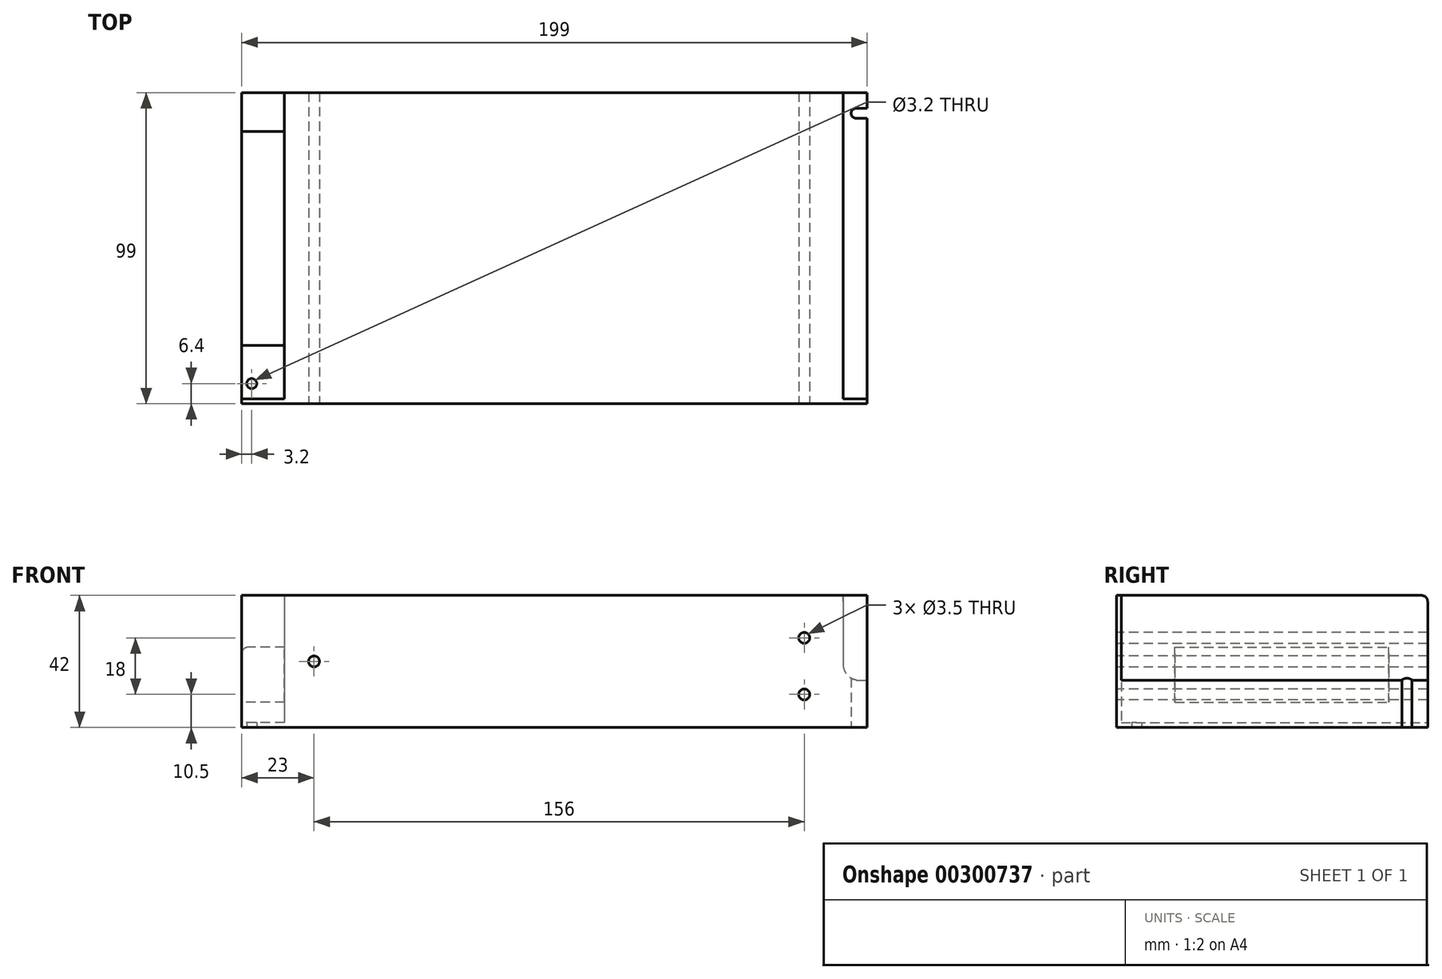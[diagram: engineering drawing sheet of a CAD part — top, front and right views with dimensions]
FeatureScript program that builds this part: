
annotation { "Feature Type Name" : "Feature", "Feature Type Description" : "" }
export const myFeature = defineFeature(function(context is Context, id is Id, definition is map)
    precondition{}
    {
        {
            var Q0;
            Q0=qCreatedBy(makeId("Top.planeOp"),FACE);
            var sketch = newSketch(context, id + "F0", { "sketchPlane" : qUnion([Q0])});
            skLineSegment(sketch, "E0.bottom", {"start": v(-99.5, 49) * mm, "end": v(99.5, 49) * mm});
            skLineSegment(sketch, "E0.top", {"start": v(-99.5, -49) * mm, "end": v(99.5, -49) * mm});
            skLineSegment(sketch, "E0.left", {"start": v(-99.5, 49) * mm, "end": v(-99.5, -49) * mm});
            skLineSegment(sketch, "E0.right", {"start": v(99.5, 49) * mm, "end": v(99.5, -49) * mm});
            skPoint(sketch, "E0.middle", {"position": v(0, 0) * mm});
            skSolve(sketch);
        }
        {
            var Q0;
            Q0=qCreatedBy(makeId("Front.planeOp"),FACE);
            var sketch = newSketch(context, id + "F1", { "sketchPlane" : qUnion([Q0])});
            skLineSegment(sketch, "E1.bottom", {"start": v(-99.5, 21) * mm, "end": v(99.5, 21) * mm});
            skLineSegment(sketch, "E1.top", {"start": v(-99.5, -21) * mm, "end": v(99.5, -21) * mm});
            skLineSegment(sketch, "E1.left", {"start": v(-99.5, 21) * mm, "end": v(-99.5, -21) * mm});
            skLineSegment(sketch, "E1.right", {"start": v(99.5, 21) * mm, "end": v(99.5, -21) * mm});
            skPoint(sketch, "E1.middle", {"position": v(0, 0) * mm});
            skCircle(sketch, "E2", {"center": v(-76.5, 0) * mm, "radius": 1.75 * mm});
            skCircle(sketch, "E3", {"center": v(79.5, 7.5) * mm, "radius": 1.75 * mm});
            skCircle(sketch, "E4.MirrorC", {"center": v(79.5, -10.5) * mm, "radius": 1.75 * mm});
            skSolve(sketch);
        }
        {
            var Q0;
            Q0=makeQuery(id+"F1.imprint","IMPRINT",FACE,{"disambiguationData":[TD([[makeQuery(id+"F1.imprint","IMPRINT",EDGE,{"derivedFrom":sQuery(id+"F1.wireOp",EDGE,"E1.bottom")}),-1.0]])]});
            extrude(context, id + "F2", {"entities" : qUnion([Q0]), "oppositeDirection" : true, "depth" : 99 * mm});
        }
        {
            var Q0;
            Q0=makeQuery(id+"F2.opExtrude","SWEPT_FACE",FACE,{"disambiguationData":[OSD([sQuery(id+"F1.wireOp",EDGE,"E1.right")])]});
            cPlane(context, id + "F3", {"entities" : qUnion([Q0]), "cplaneType" : CPlaneType.OFFSET, "offset" : 0 * mm, "width" : 150 * mm, "height" : 150 * mm});
        }
        {
            var Q0;
            Q0=qCreatedBy(id+"F3.planeOp",FACE);
            var sketch = newSketch(context, id + "F4", { "sketchPlane" : qUnion([Q0])});
            skLineSegment(sketch, "E5.bottom", {"start": v(99, 21) * mm, "end": v(1.5, 21) * mm});
            skLineSegment(sketch, "E5.top", {"start": v(99, -6) * mm, "end": v(1.5, -6) * mm});
            skLineSegment(sketch, "E5.left", {"start": v(99, 21) * mm, "end": v(99, -6) * mm});
            skLineSegment(sketch, "E5.right", {"start": v(1.5, 21) * mm, "end": v(1.5, -6) * mm});
            skSolve(sketch);
        }
        {
            var Q0;
            Q0 = qSketchRegion(id + "F4", true);
            extrude(context, id + "F5", {"entities" : qUnion([Q0]), "operationType" : NewBodyOperationType.REMOVE, "oppositeDirection" : true, "depth" : 7.6 * mm});
        }
        {
            var Q0;
            Q0=makeQuery(id+"F5.boolean.opBoolean","COPY",EDGE,{"derivedFrom":makeQuery(id+"F5.opExtrude","CAP_EDGE",EDGE,{"disambiguationData":[OSD([sQuery(id+"F4.wireOp",EDGE,"E5.top")])],"isStart":false})});
            fillet(context, id + "F6", {"entities" : qUnion([Q0]), "radius" : 5 * mm, "tangentPropagation" : true, "allowEdgeOverflow" : false});
        }
        {
            var Q0;
            Q0=makeQuery(id+"F2.opExtrude","SWEPT_FACE",FACE,{"disambiguationData":[OSD([sQuery(id+"F1.wireOp",EDGE,"E1.left")])]});
            cPlane(context, id + "F7", {"entities" : qUnion([Q0]), "cplaneType" : CPlaneType.OFFSET, "offset" : 0 * mm, "width" : 150 * mm, "height" : 150 * mm});
        }
        {
            var Q0;
            Q0=qCreatedBy(id+"F7.planeOp",FACE);
            var sketch = newSketch(context, id + "F8", { "sketchPlane" : qUnion([Q0])});
            skLineSegment(sketch, "E6.bottom", {"start": v(-1.5, 21) * mm, "end": v(-99, 21) * mm});
            skLineSegment(sketch, "E6.top", {"start": v(-1.5, -19.5) * mm, "end": v(-99, -19.5) * mm});
            skLineSegment(sketch, "E6.left", {"start": v(-1.5, 21) * mm, "end": v(-1.5, -19.5) * mm});
            skLineSegment(sketch, "E6.right", {"start": v(-99, 21) * mm, "end": v(-99, -19.5) * mm});
            skSolve(sketch);
        }
        {
            var Q0;
            Q0 = qSketchRegion(id + "F8", true);
            extrude(context, id + "F9", {"entities" : qUnion([Q0]), "operationType" : NewBodyOperationType.REMOVE, "oppositeDirection" : true, "depth" : 13.6 * mm});
        }
        {
            var Q0;
            Q0=qCreatedBy(id+"F7.planeOp",FACE);
            var sketch = newSketch(context, id + "F10", { "sketchPlane" : qUnion([Q0])});
            skLineSegment(sketch, "E7.bottom", {"start": v(-86.6, 4.5) * mm, "end": v(-18.6, 4.5) * mm});
            skLineSegment(sketch, "E7.top", {"start": v(-86.6, -13) * mm, "end": v(-18.6, -13) * mm});
            skLineSegment(sketch, "E7.left", {"start": v(-86.6, 4.5) * mm, "end": v(-86.6, -13) * mm});
            skLineSegment(sketch, "E7.right", {"start": v(-18.6, 4.5) * mm, "end": v(-18.6, -13) * mm});
            skSolve(sketch);
        }
        {
            var Q0;
            Q0 = qSketchRegion(id + "F10", true);
            extrude(context, id + "F11", {"entities" : qUnion([Q0]), "operationType" : NewBodyOperationType.ADD, "endBound" : BoundingType.UP_TO_NEXT, "oppositeDirection" : true, "depth" : 25 * mm});
        }
        {
            var Q0;
            Q0=makeQuery(id+"F11.opExtrude","CAP_EDGE",EDGE,{"disambiguationData":[OSD([sQuery(id+"F10.wireOp",EDGE,"E7.bottom")])],"isStart":true});
            fillet(context, id + "F12", {"entities" : qUnion([Q0]), "radius" : 2 * mm, "tangentPropagation" : true, "allowEdgeOverflow" : false});
        }
        {
            var Q0;
            Q0=makeQuery(id+"F2.opExtrude","CAP_EDGE",EDGE,{"disambiguationData":[OSD([sQuery(id+"F1.wireOp",EDGE,"E1.bottom")])],"isStart":false});
            fillet(context, id + "F13", {"entities" : qUnion([Q0]), "radius" : 2 * mm, "tangentPropagation" : true, "allowEdgeOverflow" : false});
        }
        {
            var Q0;
            Q0=sQuery(id+"F1.wireOp",EDGE,"E2");
            var Q1;
            Q1=sQuery(id+"F1.wireOp",EDGE,"E3");
            var Q2;
            Q2=sQuery(id+"F1.wireOp",EDGE,"E4.MirrorC");
            extrude(context, id + "F14", {"bodyType" : ToolBodyType.SURFACE, "surfaceEntities" : qUnion([Q0, Q1, Q2]), "depth" : 25 * mm});
        }
        {
            var Q0;
            Q0=makeQuery(id+"F2.opExtrude","SWEPT_FACE",FACE,{"disambiguationData":[OSD([sQuery(id+"F1.wireOp",EDGE,"E1.top")])]});
            var sketch = newSketch(context, id + "F15", { "sketchPlane" : qUnion([Q0])});
            skCircle(sketch, "E8", {"center": v(-96.3, -6.4) * mm, "radius": 1.6 * mm});
            skLineSegment(sketch, "E9.bottom", {"start": v(99.5, -94) * mm, "end": v(96, -94) * mm});
            skLineSegment(sketch, "E9.top", {"start": v(99.5, -90.8) * mm, "end": v(96, -90.8) * mm});
            skLineSegment(sketch, "E9.left", {"start": v(99.5, -94) * mm, "end": v(99.5, -90.8) * mm});
            skLineSegment(sketch, "E9.right", {"start": v(96, -94) * mm, "end": v(96, -90.8) * mm});
            skCircle(sketch, "E10", {"center": v(96, -92.4) * mm, "radius": 1.6 * mm});
            skSolve(sketch);
        }
        {
            var Q0;
            Q0=makeQuery(id+"F15.imprint","IMPRINT",FACE,{"disambiguationData":[TD([[makeQuery(id+"F15.imprint","IMPRINT",EDGE,{"derivedFrom":sQuery(id+"F15.wireOp",EDGE,"E8")}),1.0]])]});
            var Q1;
            {var subQ0=sQuery(id+"F15.wireOp",EDGE,"E9.bottom");Q1=makeQuery(id+"F15.imprint","IMPRINT",FACE,{"disambiguationData":[TD([[makeQuery(id+"F15.imprint","IMPRINT",EDGE,{"derivedFrom":subQ0}),-1.0]])]});}
            var Q2;
            {var subQ0=sQuery(id+"F15.wireOp",EDGE,"E9.right");Q2=makeQuery(id+"F15.imprint","IMPRINT",FACE,{"disambiguationData":[TD([[makeQuery(id+"F15.imprint","IMPRINT",EDGE,{"derivedFrom":subQ0}),-1.0]])]});}
            var Q3;
            {var subQ0=sQuery(id+"F15.wireOp",EDGE,"E9.right");Q3=makeQuery(id+"F15.imprint","IMPRINT",FACE,{"disambiguationData":[TD([[makeQuery(id+"F15.imprint","IMPRINT",EDGE,{"derivedFrom":subQ0}),1.0]])]});}
            var Q4;
            Q4=sQuery(id+"F15.wireOp",EDGE,"E8");
            var Q5;
            Q5=sQuery(id+"F15.wireOp",EDGE,"E10");
            var Q6;
            Q6=sQuery(id+"F15.wireOp",EDGE,"E9.top");
            var Q7;
            Q7=sQuery(id+"F15.wireOp",EDGE,"E9.bottom");
            var Q8;
            Q8=sQuery(id+"F15.wireOp",EDGE,"E9.left");
            extrude(context, id + "F16", {"entities" : qUnion([Q0, Q1, Q2, Q3]), "operationType" : NewBodyOperationType.REMOVE, "surfaceEntities" : qUnion([Q4, Q5, Q6, Q7, Q8]), "endBound" : BoundingType.THROUGH_ALL, "oppositeDirection" : true, "depth" : 25 * mm});
        }
    });
